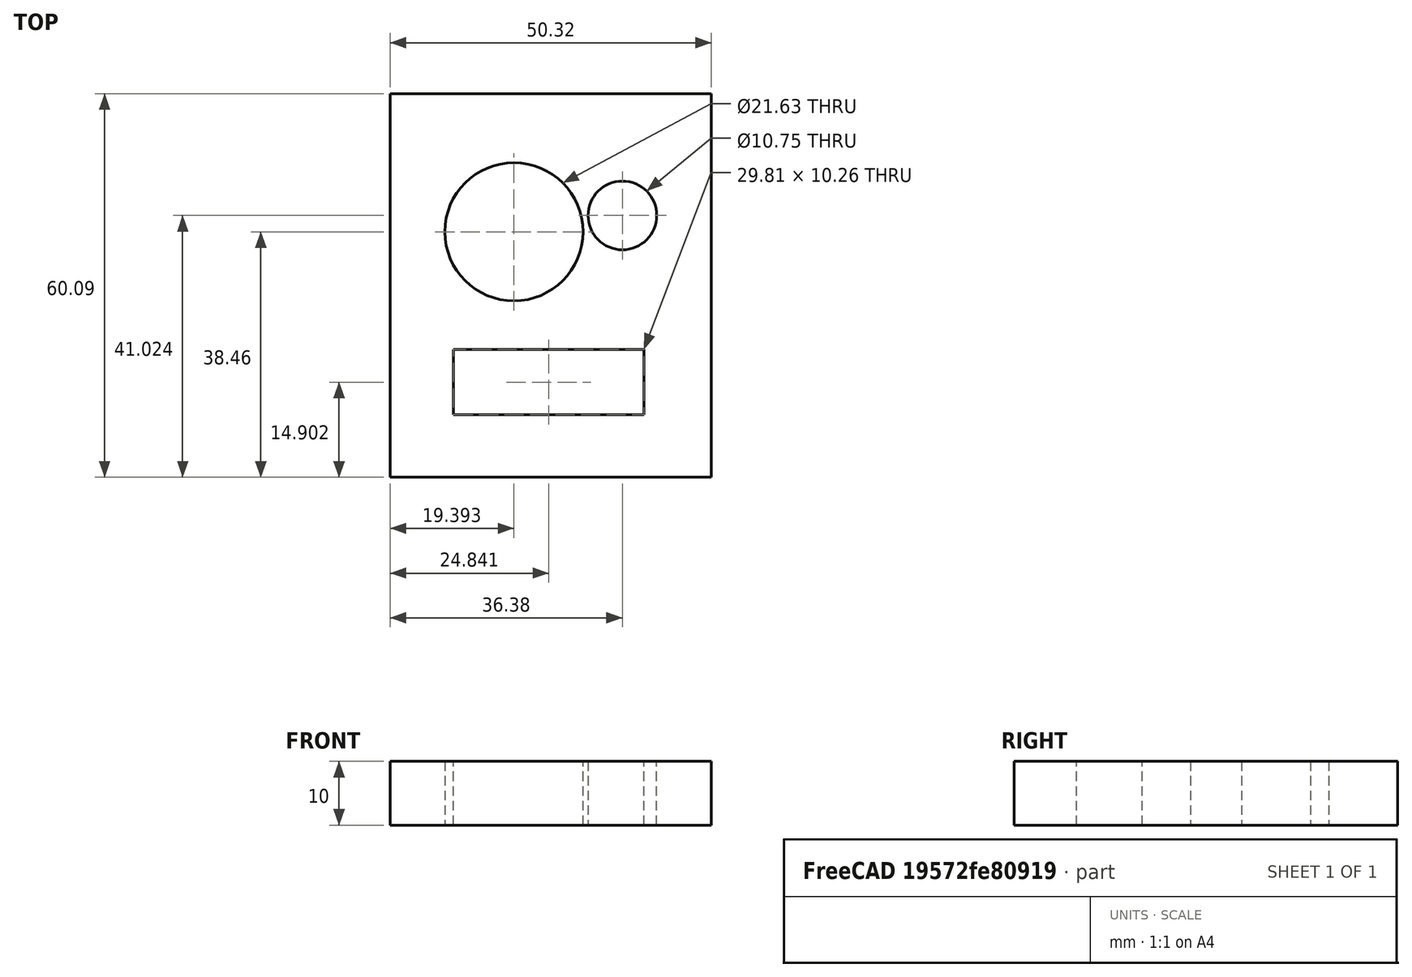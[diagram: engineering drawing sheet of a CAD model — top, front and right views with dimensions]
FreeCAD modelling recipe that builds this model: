
FCSTD DOCUMENT  (FreeCAD 0.20R29177 +233 (Git))
Label: robot
License: All rights reserved
LicenseURL: http://en.wikipedia.org/wiki/All_rights_reserved
objects: Part::Extrusion×2, Sketcher::SketchObject×1
note: 3 computed .brp shape members not serialized (recipe doc carries the construction recipe); baked Part::Feature solids carry a one-line shape summary decoded from their .brp

FEATURE [Sketcher::SketchObject] Sketch
  FullyConstrained = false
  sketch-geometry (10):
    g0: LineSegment StartX=-30.2078 StartY=40.0641 StartZ=0 EndX=-30.2083 EndY=-20.0321 EndZ=0
    g1: LineSegment StartX=-30.2083 StartY=-20.0321 StartZ=0 EndX=20.1122 EndY=-20.0321 EndZ=0
    g2: LineSegment StartX=20.1122 StartY=-20.0321 StartZ=0 EndX=20.1122 EndY=40.0679 EndZ=0
    g3: LineSegment StartX=20.1122 StartY=40.0641 StartZ=0 EndX=-30.2078 EndY=40.0641 EndZ=0
    g4: Circle CenterX=-10.8173 CenterY=18.4295 CenterZ=0 NormalX=0 NormalY=0 NormalZ=1 AngleXU=0 Radius=10.815
    g5: Circle CenterX=6.16987 CenterY=20.9936 CenterZ=0 NormalX=0 NormalY=0 NormalZ=1 AngleXU=0 Radius=5.375
    g6: LineSegment StartX=-20.2724 StartY=0 StartZ=0 EndX=-20.2747 EndY=-10.26 EndZ=0
    g7: LineSegment StartX=-20.2747 StartY=-10.26 StartZ=0 EndX=9.53525 EndY=-10.2564 EndZ=0
    g8: LineSegment StartX=9.53525 StartY=-10.2564 StartZ=0 EndX=9.53525 EndY=0 EndZ=0
    g9: LineSegment StartX=9.53525 StartY=0 StartZ=0 EndX=-20.2724 EndY=0 EndZ=0
  constraints (13):
    c: Coincident(g1,g0)
    c: Coincident(g3,g0)
    c: PointOnObject(g6,g-1)
    c: Coincident(g7,g6)
    c: Coincident(g8,g7)
    c: Coincident(g9,g8)
    c: Coincident(g9,g6)
    c: DistanceY(g2,g2) = 60.1
    c: DistanceX(g3,g3) = 50.32
    c: Diameter(g4) = 21.63
    c: Diameter(g5) = 10.75
    c: DistanceY(g6,g6) = 10.26
    c: DistanceX(g7,g7) = 29.81
FEATURE [Part::Extrusion] Extrude
  Base = -> Sketch
  Dir = (0,0,1)
  DirMode = 2
  FaceMakerClass = Part::FaceMakerBullseye
  LengthFwd = 10
  LengthRev = 0
  Solid = true
  Symmetric = false
FEATURE [Part::Extrusion] Extrude001
  Base = -> Sketch
  Dir = (0,0,1)
  DirMode = 2
  FaceMakerClass = Part::FaceMakerBullseye
  LengthFwd = 10
  LengthRev = 0
  Solid = true
  Symmetric = false
